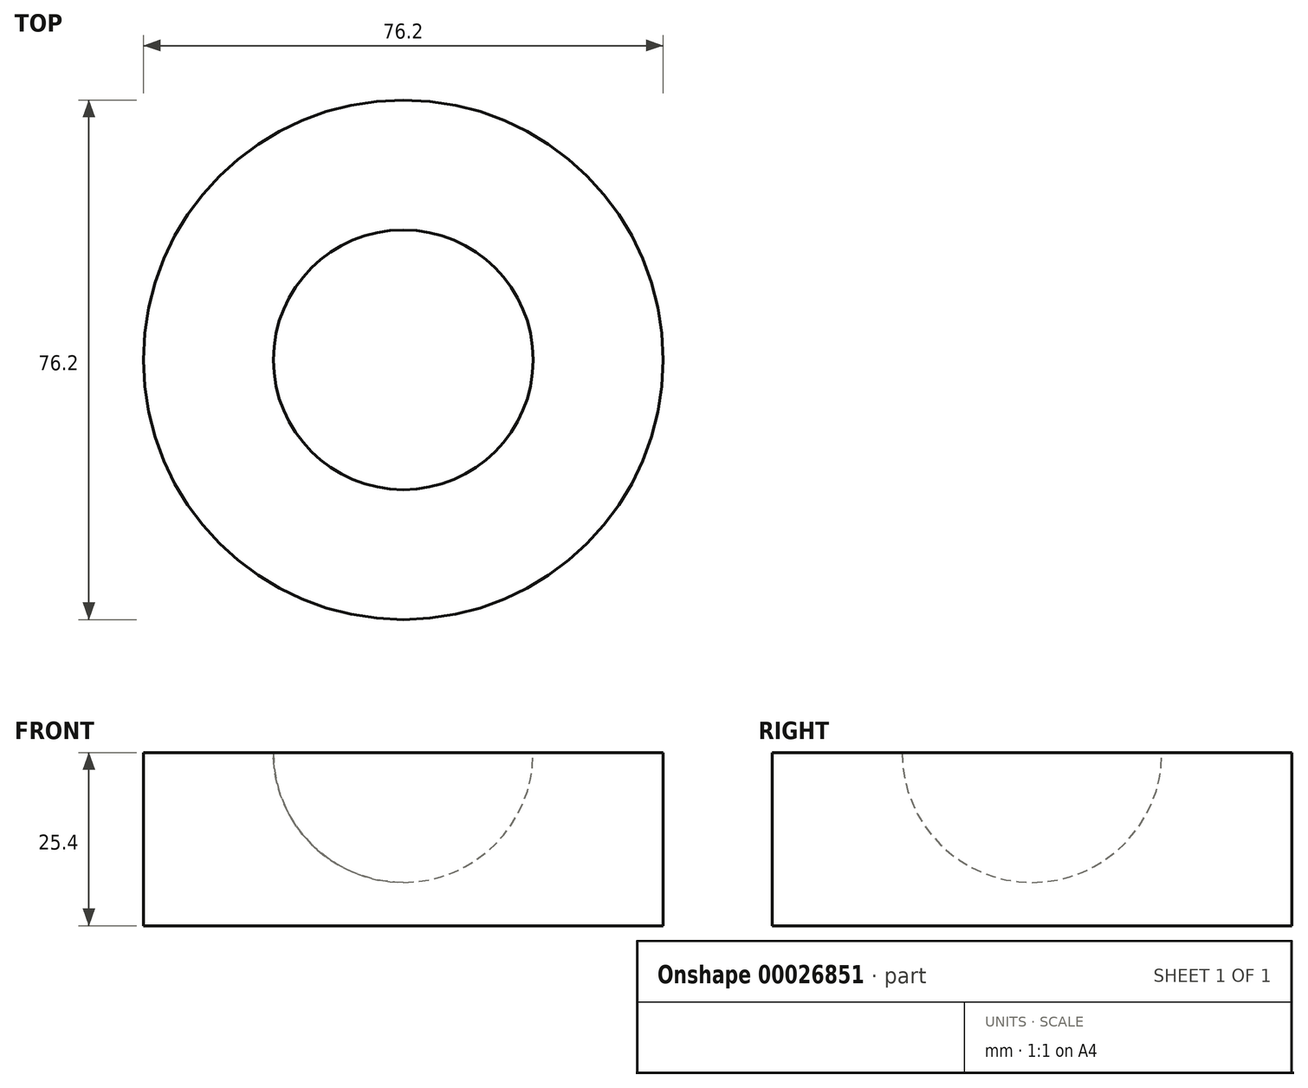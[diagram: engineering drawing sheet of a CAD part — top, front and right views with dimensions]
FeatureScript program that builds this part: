
annotation { "Feature Type Name" : "Feature", "Feature Type Description" : "" }
export const myFeature = defineFeature(function(context is Context, id is Id, definition is map)
    precondition{}
    {
        {
            var Q0;
            Q0=qCreatedBy(makeId("Front.planeOp"),FACE);
            var sketch = newSketch(context, id + "F0", { "sketchPlane" : qUnion([Q0])});
            skLineSegment(sketch, "E0.bottom", {"start": v(18.87, 25.4) * mm, "end": v(38.1, 25.4) * mm});
            skLineSegment(sketch, "E0.top", {"start": v(0, 0) * mm, "end": v(38.1, 0) * mm});
            skLineSegment(sketch, "E0.left", {"start": v(0, 6.35) * mm, "end": v(0, 0) * mm});
            skLineSegment(sketch, "E0.right", {"start": v(38.1, 25.4) * mm, "end": v(38.1, 0) * mm});
            skArc(sketch, "E1", {"start": v(0, 6.35) * mm, "mid": v(13.47, 11.93) * mm, "end": v(19.05, 25.4) * mm});
            skSolve(sketch);
        }
        {
            var Q0;
            Q0=makeQuery(id+"F0.imprint","IMPRINT",FACE,{"disambiguationData":[TD([[makeQuery(id+"F0.imprint","IMPRINT",EDGE,{"derivedFrom":sQuery(id+"F0.wireOp",EDGE,"E0.bottom")}),-1.0]])]});
            var Q1;
            Q1=sQuery(id+"F0.wireOp",EDGE,"E0.left");
            revolve(context, id + "F1", {"entities" : qUnion([Q0]), "axis" : qUnion([Q1]), "revolveType" : RevolveType.FULL});
        }
    });
